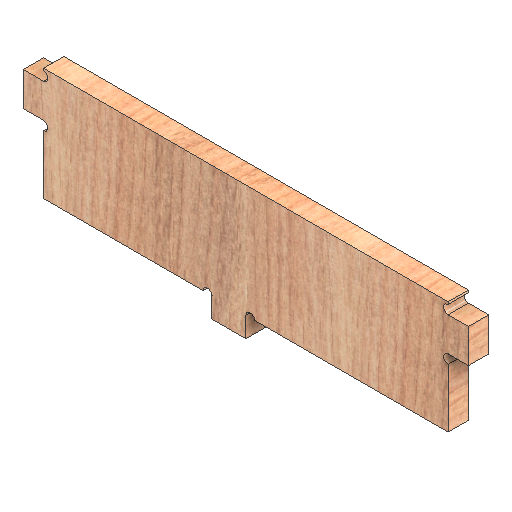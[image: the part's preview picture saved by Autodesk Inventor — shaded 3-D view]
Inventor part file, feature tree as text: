
AUTODESK INVENTOR PART (.ipt)
format: ipt  version: 2021 (Build 250183000, 183)  size: 270,848 bytes
history: native  units: mm
features: other x2, sketch x1, hole x1, extrude x1
ambient origin geometry x8: Origin, YZ Plane, XZ Plane, XY Plane, X Axis, Y Axis, Z Axis, Center Point
bodies: Solid1 (feature_tree)
feature tree (5):
  sketch  "Sketch1"  dims[d36=18.0mm d37=0.0mm]
  other  "CONTOURS"
  hole  "HOLES"  [1 undecoded]
  other  "LETTERS"
  extrude  "Extrusion1"  [1 undecoded]
note: 2 required parameter values undecoded (feature->parameter linkage not recoverable at this tier; creation-order binding heuristic only, values carry confidence <= 0.55)
